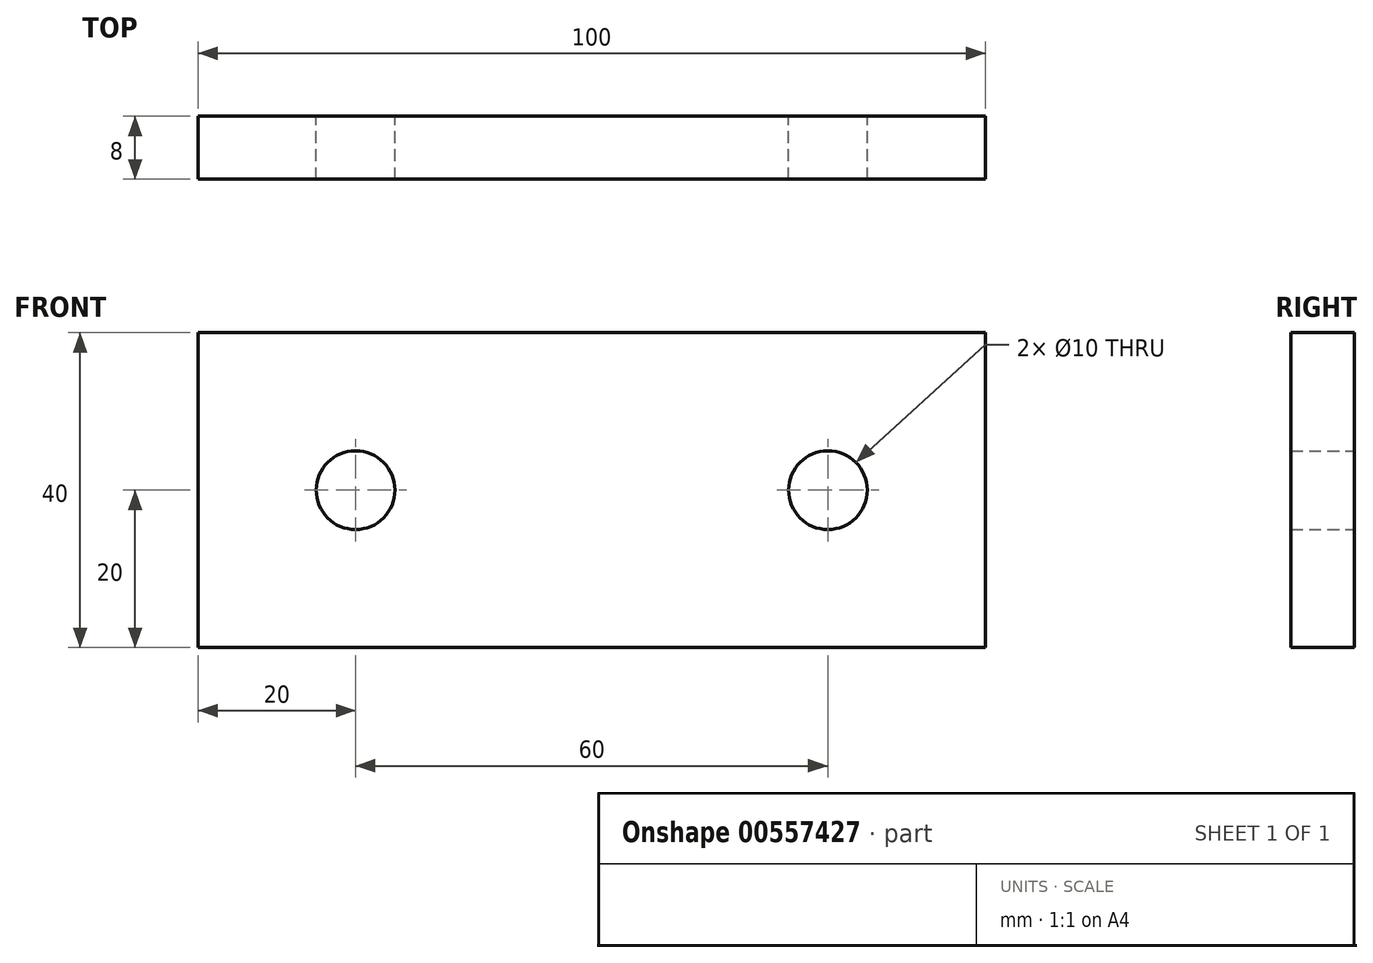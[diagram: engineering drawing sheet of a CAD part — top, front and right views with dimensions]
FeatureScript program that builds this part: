
annotation { "Feature Type Name" : "Feature", "Feature Type Description" : "" }
export const myFeature = defineFeature(function(context is Context, id is Id, definition is map)
    precondition{}
    {
        {
            var Q0;
            Q0=qCreatedBy(makeId("Front.planeOp"),FACE);
            var sketch = newSketch(context, id + "F0", { "sketchPlane" : qUnion([Q0])});
            skLineSegment(sketch, "E0.bottom", {"start": v(50, 20) * mm, "end": v(-50, 20) * mm});
            skLineSegment(sketch, "E0.top", {"start": v(50, -20) * mm, "end": v(-50, -20) * mm});
            skLineSegment(sketch, "E0.left", {"start": v(50, 20) * mm, "end": v(50, -20) * mm});
            skLineSegment(sketch, "E0.right", {"start": v(-50, 20) * mm, "end": v(-50, -20) * mm});
            skPoint(sketch, "E0.middle", {"position": v(0, 0) * mm});
            skCircle(sketch, "E1", {"center": v(-30, 0) * mm, "radius": 5 * mm});
            skCircle(sketch, "E2", {"center": v(30, 0) * mm, "radius": 5 * mm});
            skSolve(sketch);
        }
        {
            var Q0;
            Q0=makeQuery(id+"F0.imprint","IMPRINT",FACE,{"disambiguationData":[TD([[makeQuery(id+"F0.imprint","IMPRINT",EDGE,{"derivedFrom":sQuery(id+"F0.wireOp",EDGE,"E0.bottom")}),1.0]])]});
            extrude(context, id + "F1", {"entities" : qUnion([Q0]), "endBound" : BoundingType.SYMMETRIC, "depth" : 8 * mm, "offsetDistance" : 25 * mm});
        }
    });
